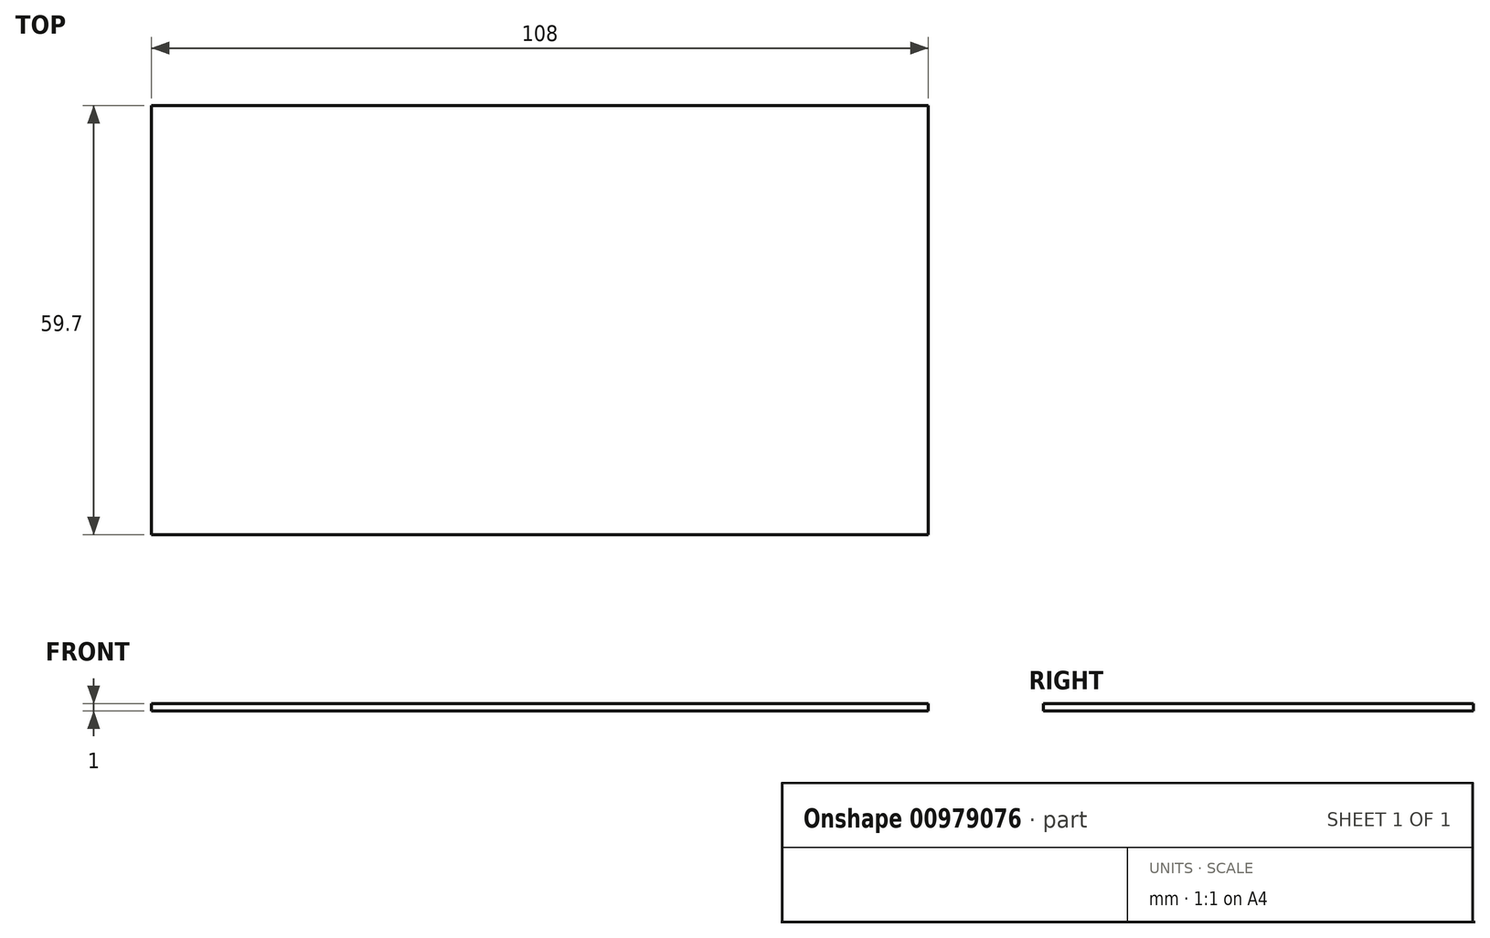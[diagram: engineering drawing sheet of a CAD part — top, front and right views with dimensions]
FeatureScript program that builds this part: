
annotation { "Feature Type Name" : "Feature", "Feature Type Description" : "" }
export const myFeature = defineFeature(function(context is Context, id is Id, definition is map)
    precondition{}
    {
        {
            var Q0;
            Q0=qCreatedBy(makeId("Top.planeOp"),FACE);
            var sketch = newSketch(context, id + "F0", { "sketchPlane" : qUnion([Q0])});
            skLineSegment(sketch, "E0.bottom", {"start": v(54, -29.85) * mm, "end": v(-54, -29.85) * mm});
            skLineSegment(sketch, "E0.top", {"start": v(54, 29.85) * mm, "end": v(-54, 29.85) * mm});
            skLineSegment(sketch, "E0.left", {"start": v(54, -29.85) * mm, "end": v(54, 29.85) * mm});
            skLineSegment(sketch, "E0.right", {"start": v(-54, -29.85) * mm, "end": v(-54, 29.85) * mm});
            skPoint(sketch, "E0.middle", {"position": v(0, 0) * mm});
            skSolve(sketch);
        }
        {
            var Q0;
            Q0=makeQuery(id+"F0.imprint","IMPRINT",FACE,{"disambiguationData":[TD([[makeQuery(id+"F0.imprint","IMPRINT",EDGE,{"derivedFrom":sQuery(id+"F0.wireOp",EDGE,"E0.bottom")}),-1.0]])]});
            extrude(context, id + "F1", {"entities" : qUnion([Q0]), "depth" : 1 * mm, "offsetDistance" : 25.4 * mm});
        }
    });
